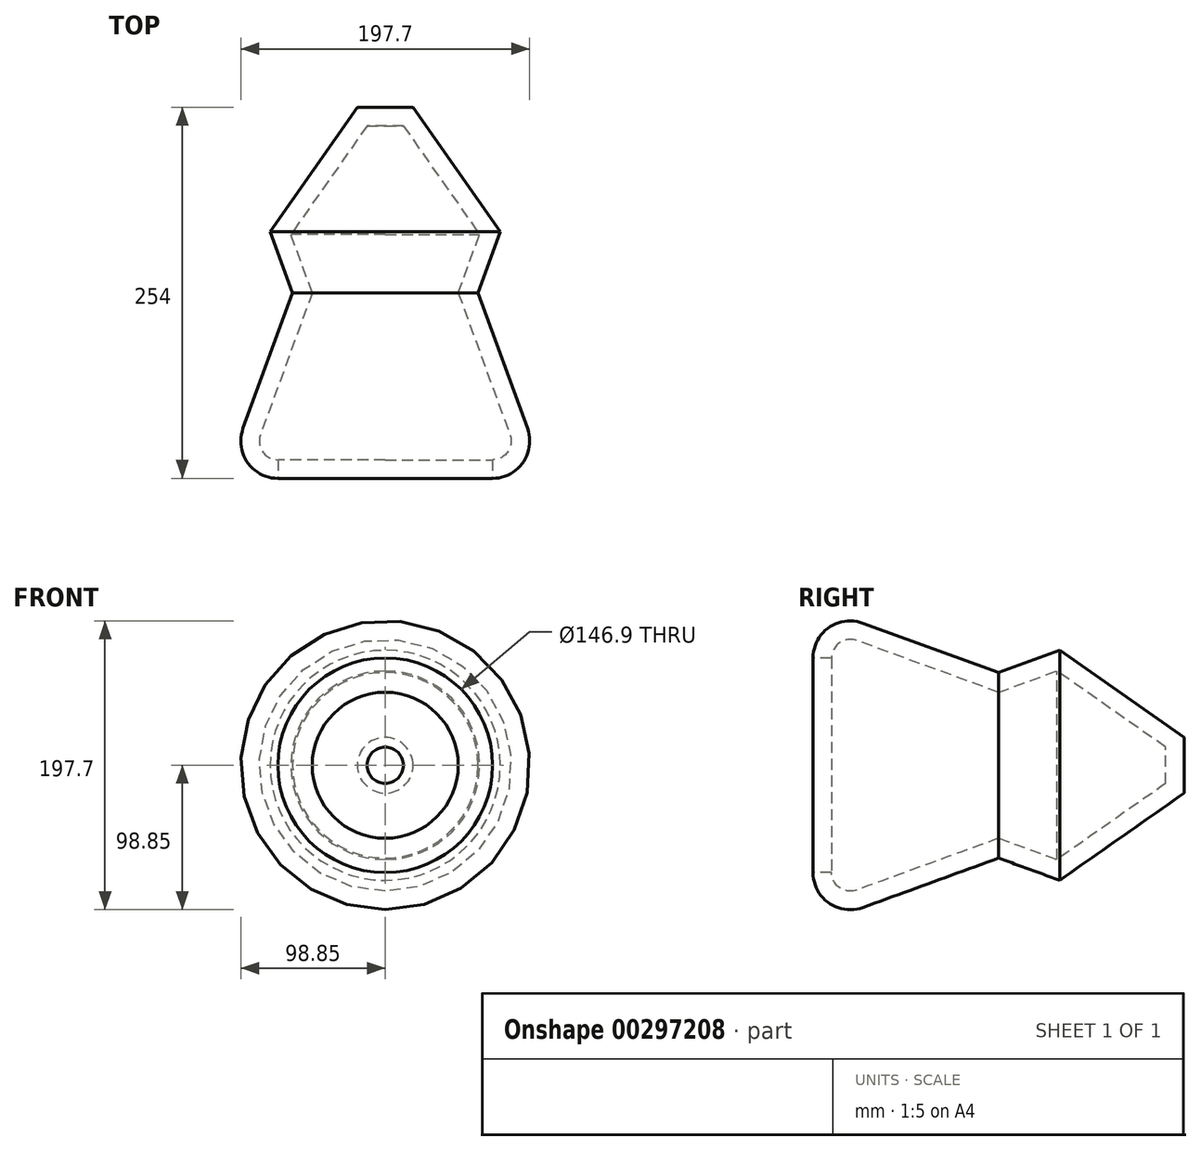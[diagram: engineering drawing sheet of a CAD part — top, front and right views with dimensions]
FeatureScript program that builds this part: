
annotation { "Feature Type Name" : "Feature", "Feature Type Description" : "" }
export const myFeature = defineFeature(function(context is Context, id is Id, definition is map)
    precondition{}
    {
        {
            var Q0;
            Q0=qCreatedBy(makeId("Front.planeOp"),FACE);
            var sketch = newSketch(context, id + "F0", { "sketchPlane" : qUnion([Q0])});
            skCircle(sketch, "E0", {"center": v(0, 0) * mm, "radius": 63.5 * mm});
            skSolve(sketch);
        }
        {
            var Q0;
            Q0=makeQuery(id+"F0.imprint","IMPRINT",FACE,{"disambiguationData":[TD([[makeQuery(id+"F0.imprint","IMPRINT",EDGE,{"derivedFrom":sQuery(id+"F0.wireOp",EDGE,"E0")}),1.0]])]});
            var Q1;
            Q1=sQuery(id+"F0.wireOp",EDGE,"E0");
            extrude(context, id + "F1", {"entities" : qUnion([Q0]), "surfaceEntities" : qUnion([Q1]), "endBound" : BoundingType.SYMMETRIC, "depth" : 254 * mm, "hasDraft" : true, "draftAngle" : 20 * degree});
        }
        {
            var Q0;
            Q0=makeQuery(id+"F1.opExtrude","CAP_EDGE",EDGE,{"disambiguationData":[OSD([sQuery(id+"F0.wireOp",EDGE,"E0")])],"isStart":false});
            fillet(context, id + "F2", {"entities" : qUnion([Q0]), "radius" : 25.4 * mm, "tangentPropagation" : true, "allowEdgeOverflow" : false});
        }
        {
            var Q0;
            Q0=makeQuery(id+"F1.opExtrude","CAP_EDGE",EDGE,{"disambiguationData":[OSD([sQuery(id+"F0.wireOp",EDGE,"E0")])],"isStart":true});
            chamfer(context, id + "F3", {"entities" : qUnion([Q0]), "width" : 63.5 * mm, "tangentPropagation" : true});
        }
        {
            var Q0;
            Q0=makeQuery(id+"F1.opExtrude","CAP_FACE",FACE,{"disambiguationData":[OSD([sQuery(id+"F0.wireOp",EDGE,"E0")])],"isStart":false});
            shell(context, id + "F4", {"entities" : qUnion([Q0]), "thickness" : 12.7 * mm});
        }
    });
